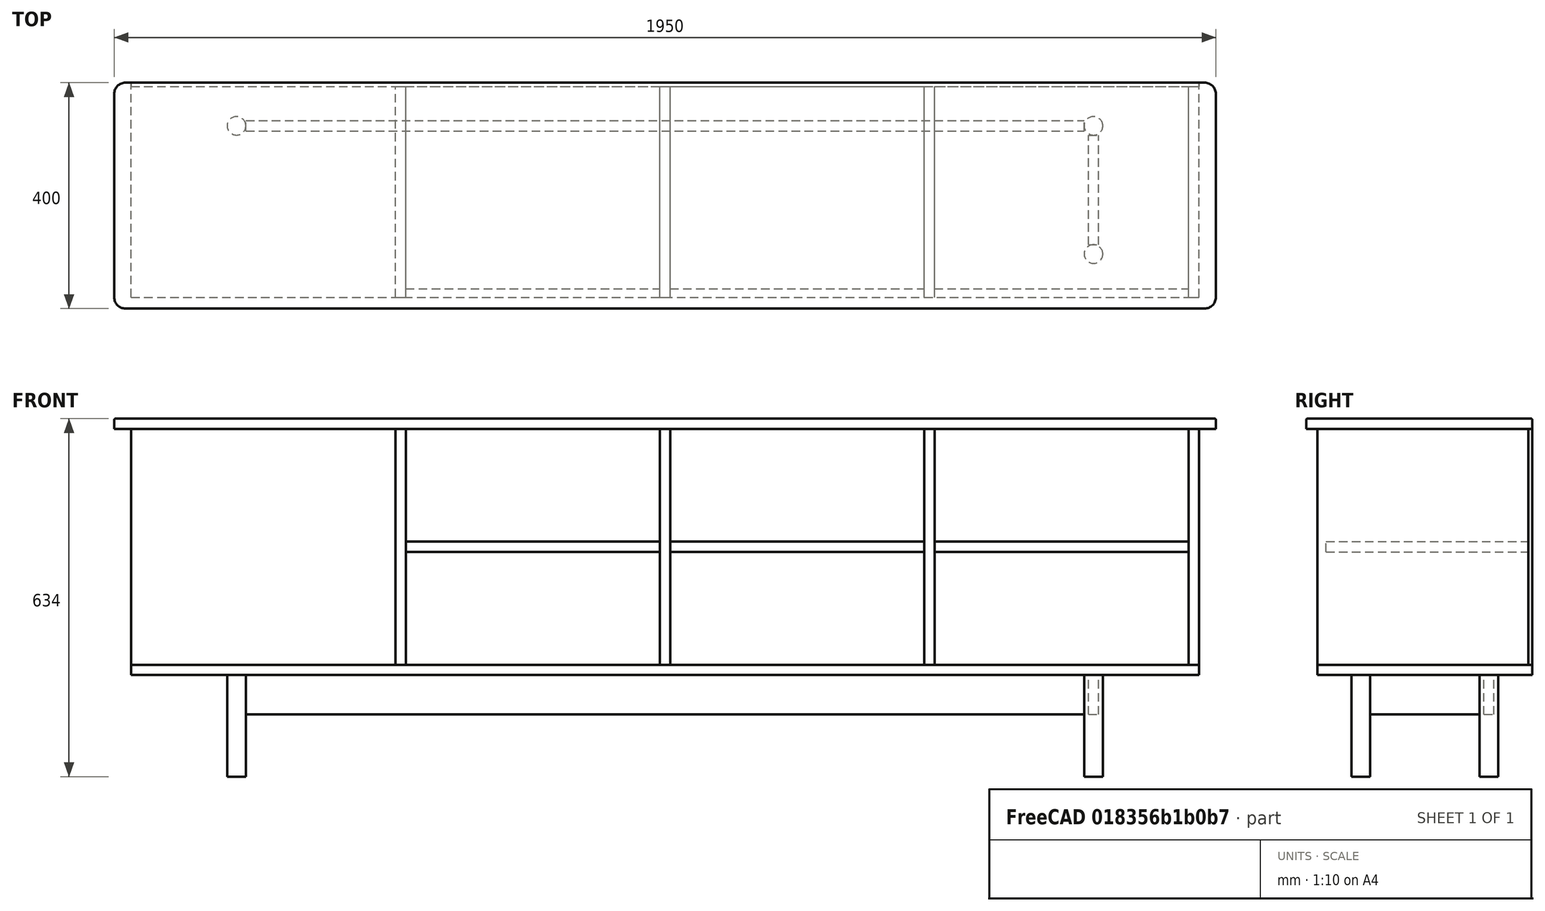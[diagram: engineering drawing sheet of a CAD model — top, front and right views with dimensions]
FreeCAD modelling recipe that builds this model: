
FCSTD DOCUMENT  (FreeCAD 0.20RUnknown)
Label: tv-furniture
License: All rights reserved
LicenseURL: http://en.wikipedia.org/wiki/All_rights_reserved
objects: Part::FeaturePython×12, Part::Box×7, Spreadsheet::Sheet×2, Part::Fillet×2, Part::Cylinder×1, TechDraw::DrawSVGTemplate×1, TechDraw::DrawViewSpreadsheet×1, TechDraw::DrawPage×1
note: 22 computed .brp shape members not serialized (recipe doc carries the construction recipe); baked Part::Feature solids carry a one-line shape summary decoded from their .brp

FEATURE [Part::Box] Box028  label="Top"
  AttacherType = Attacher::AttachEngine3D
  Height = 18
  Length = 1950
  Placement = pos=(-30,-20,436) rot=(0,0,1;0rad)
  Texture_Fit = biggest surface
  Texture_Repeat_X = 1
  Texture_Repeat_Y = 1
  Texture_Rotation = 0
  Texture_URL = <userpath>/Hentet/grantræ.jpg
  Width = 400
  expr: .Placement.Base.x = -<<Spreadsheet>>.TopBreddeMargin
  expr: .Placement.Base.y = -<<Spreadsheet>>.TopDybdeMargin
  expr: .Placement.Base.z = <<Spreadsheet>>.Hoejde - <<Spreadsheet>>.Plade
  expr: Height = <<Spreadsheet>>.TopPlade
  expr: Length = <<Spreadsheet>>.Bredde + 2 * <<Spreadsheet>>.TopBreddeMargin
FEATURE [Part::Box] Box029  label="Side/Skillevæg"
  AttacherType = Attacher::AttachEngine3D
  Height = 418
  Length = 18
  Placement = pos=(0,0,18) rot=(0,0,1;0rad)
  Texture_Fit = biggest surface
  Texture_Repeat_X = 1
  Texture_Repeat_Y = 1
  Texture_Rotation = 0
  Texture_URL = <userpath>/Hentet/grantræ.jpg
  Width = 373
  expr: .Placement.Base.z = <<Spreadsheet>>.Plade
  expr: Height = <<Spreadsheet>>.Hoejde - <<Spreadsheet>>.Plade * 2
  expr: Length = <<Spreadsheet>>.Plade
  expr: Width = <<Spreadsheet>>.Dybde - <<Spreadsheet>>.BagPlade
FEATURE [Part::Box] Box034  label="Hylde"
  AttacherType = Attacher::AttachEngine3D
  Height = 18
  Length = 450
  Placement = pos=(18,15,218) rot=(0,0,1;0rad)
  Texture_Fit = biggest surface
  Texture_Repeat_X = 1
  Texture_Repeat_Y = 1
  Texture_Rotation = 0
  Texture_URL = <userpath>/Hentet/grantræ.jpg
  Width = 358
  expr: .Placement.Base.x = <<Side/Skillevæg>>.Placement.Base.x + <<Spreadsheet>>.Plade
  expr: .Placement.Base.y = <<Spreadsheet>>.HyldeMellemrum
  expr: .Placement.Base.z = <<Spreadsheet>>.Plade + <<Spreadsheet>>.KasseHoejde
  expr: Height = <<Spreadsheet>>.Plade
  expr: Length = <<Spreadsheet>>.KasseBredde
  expr: Width = <<Spreadsheet>>.Dybde - <<Spreadsheet>>.HyldeMellemrum - <<Spreadsheet>>.BagPlade
FEATURE [Part::Box] Box035  label="Bund"
  AttacherType = Attacher::AttachEngine3D
  Height = 18
  Length = 1890
  Texture_Fit = biggest surface
  Texture_Repeat_X = 1
  Texture_Repeat_Y = 1
  Texture_Rotation = 0
  Texture_URL = <userpath>/Hentet/grantræ.jpg
  Width = 380
  expr: .Placement.Base.z = 0
  expr: Height = <<Spreadsheet>>.Plade
  expr: Length = <<Spreadsheet>>.Bredde
  expr: Width = <<Spreadsheet>>.Dybde
FEATURE [Part::Box] Box039  label="Sokkel X"
  AttacherType = Attacher::AttachEngine3D
  Height = 70
  Length = 1484
  Placement = pos=(203,67.5,-70) rot=(0,0,1;0rad)
  Texture_Fit = biggest surface
  Texture_Repeat_X = 1
  Texture_Repeat_Y = 1
  Texture_Rotation = 0
  Texture_URL = <userpath>/Hentet/grantræ.jpg
  Width = 18
  expr: .Placement.Base.x = <<Ben>>.Placement.Base.x + <<Ben>>.Radius
  expr: .Placement.Base.y = <<Ben>>.Placement.Base.y - <<Spreadsheet>>.Plade / 2
  expr: .Placement.Base.z = -<<Spreadsheet>>.SokkelHoejde
  expr: Height = <<Spreadsheet>>.SokkelHoejde
  expr: Length = <<Ben002>>.Placement.Base.x - <<Ben>>.Placement.Base.x - 2 * <<Spreadsheet>>.BenRadius
  expr: Width = <<Spreadsheet>>.Plade
FEATURE [Part::Cylinder] Cylinder008  label="Ben"
  Angle = 360
  AttacherType = Attacher::AttachEngine3D
  FirstAngle = 0
  Height = 180
  Placement = pos=(186.5,76.5,-180) rot=(0,0,1;0rad)
  Radius = 16.5
  SecondAngle = 0
  Texture_Fit = biggest surface
  Texture_Repeat_X = 1
  Texture_Repeat_Y = 1
  Texture_Rotation = 0
  Texture_URL = <userpath>/Hentet/grantræ.jpg
  expr: .Placement.Base.x = <<Spreadsheet>>.SokkelBreddeMargin + Radius
  expr: .Placement.Base.y = <<Spreadsheet>>.SokkelDybdeMargin + Radius
  expr: .Placement.Base.z = -<<Spreadsheet>>.BenHoejde
  expr: Radius = Spreadsheet002.BenRadius
FEATURE [Spreadsheet::Sheet] Spreadsheet002  label="Spreadsheet"
  cells = A1=Kassebredde; B1=Kassehøjde; C1=Dybde; D1=Plade; E1=Grundbredde; F1=Grundhøjde; G1=Topplade breddemargin; H1=Topplade dybdemargin; I1=Sokkel højde; J1=Sokkel breddemargin; K1=Sokkel dybdemargin; A2(KasseBredde)==45cm; B2(KasseHoejde)==20cm; C2(Dybde)==38cm; D2(Plade)==1.8cm; E2(Bredde)==A2 * 4 + D2 * 5; F2(Hoejde)==B2 * 2 + D2 * 3; G2(TopBreddeMargin)==3cm; H2(TopDybdeMargin)==2cm; I2(SokkelHoejde)==7cm; J2(SokkelBreddeMargin)==17cm; K2(SokkelDybdeMargin)==6cm; D3(TopPlade)==18mm; A4=Benhøjde; B4=Ben radius; D4(BagPlade)==7mm; A5(BenHoejde)==18cm; B5(BenRadius)==33mm / 2; A7=Hylde mellemrum; A8(HyldeMellemrum)==1.5cm; A13=Type; B13=Mål; C13=Antal; D13=Bauhaus; E13=Silvan; A14=Limtræ; B14=400*2000*18; C14=4; D14==229.95 * C14; E14==C14 * 229.95; A15=Finér bauhaus; B15=800*1200*6; C15=2; D15==189.95 * C15; A16=Finér silvan; B16=2440*1220*6,5; C16=1; E16==C16 * 339.95; A17=Rundstok; B17=Ø33 x 2100; C17=1; D17==C17 * 124.95; E17=129.95; A19=I alt; D19==D14 + D15 + D17; E19==E14 + E16 + E17
FEATURE [Part::Box] panelXY  label="Bagplade"
  AttacherType = Attacher::AttachEngine3D
  Height = 7
  Length = 1890
  Placement = pos=(0,380,18) rot=(1,0,0;1.5708rad)
  Texture_Fit = biggest surface
  Texture_Repeat_X = 1
  Texture_Repeat_Y = 1
  Texture_Rotation = 0
  Texture_URL = <userpath>/Hentet/grantræ.jpg
  Width = 418
  expr: .Placement.Base.y = <<Spreadsheet>>.Dybde
  expr: .Placement.Base.z = <<Spreadsheet>>.Plade
  expr: Height = <<Spreadsheet>>.BagPlade
  expr: Length = <<Spreadsheet>>.Bredde
  expr: Width = <<Spreadsheet>>.KasseHoejde * 2 + <<Spreadsheet>>.Plade
FEATURE [Part::Box] Box041  label="Sokkel Y"
  AttacherType = Attacher::AttachEngine3D
  Height = 70
  Length = 18
  Placement = pos=(177.5,93,-70) rot=(0,0,1;0rad)
  Texture_Fit = biggest surface
  Texture_Repeat_X = 1
  Texture_Repeat_Y = 1
  Texture_Rotation = 0
  Texture_URL = <userpath>/Hentet/grantræ.jpg
  Width = 194
  expr: .Placement.Base.x = <<Ben001>>.Placement.Base.x - <<Spreadsheet>>.Plade / 2
  expr: .Placement.Base.y = <<Ben>>.Placement.Base.y + <<Spreadsheet>>.BenRadius
  expr: .Placement.Base.z = -<<Spreadsheet>>.SokkelHoejde
  expr: Height = <<Spreadsheet>>.SokkelHoejde
  expr: Length = <<Spreadsheet>>.Plade
  expr: Width = <<Ben001>>.Placement.Base.y - <<Ben>>.Placement.Base.y - 2 * <<Spreadsheet>>.BenRadius
FEATURE [Part::Fillet] Fillet004
  Base = -> Box028
  Edges = 4 edges r=20: [Edge1,Edge3,Edge5,Edge7]
FEATURE [Part::Fillet] Fillet005
  Base = -> Fillet004
  Edges = 8 edges r=2: [Edge1,Edge5,Edge6,Edge7,Edge8,Edge9,Edge10,Edge11]
FEATURE [Part::FeaturePython] Clone  label="Side/Skillevæg001"  # Draft clone (typed FeaturePython)
  AttacherType = Attacher::AttachEngine3D
  Fuse = false
  Objects = -> [Box029]
  Placement = pos=(468,0,18) rot=(0,0,1;0rad)
  Scale = (1,1,1)
  expr: .Placement.Base.x = <<Spreadsheet>>.Plade + <<Spreadsheet>>.KasseBredde
  expr: .Placement.Base.z = <<Spreadsheet>>.Plade
FEATURE [Part::FeaturePython] Clone001  label="Side/Skillevæg002"  # Draft clone (typed FeaturePython)
  AttacherType = Attacher::AttachEngine3D
  Fuse = false
  Objects = -> [Box029]
  Placement = pos=(936,0,18) rot=(0,0,1;0rad)
  Scale = (1,1,1)
  expr: .Placement.Base.x = <<Spreadsheet>>.Plade * 2 + <<Spreadsheet>>.KasseBredde * 2
  expr: .Placement.Base.z = <<Spreadsheet>>.Plade
FEATURE [Part::FeaturePython] Clone002  label="Side/Skillevæg003"  # Draft clone (typed FeaturePython)
  AttacherType = Attacher::AttachEngine3D
  Fuse = false
  Objects = -> [Box029]
  Placement = pos=(1404,0,18) rot=(0,0,1;0rad)
  Scale = (1,1,1)
  expr: .Placement.Base.x = <<Spreadsheet>>.Plade * 3 + <<Spreadsheet>>.KasseBredde * 3
  expr: .Placement.Base.z = <<Spreadsheet>>.Plade
FEATURE [Part::FeaturePython] Clone003  label="Side/Skillevæg004"  # Draft clone (typed FeaturePython)
  AttacherType = Attacher::AttachEngine3D
  Fuse = false
  Objects = -> [Box029]
  Placement = pos=(1872,0,18) rot=(0,0,1;0rad)
  Scale = (1,1,1)
  expr: .Placement.Base.x = <<Spreadsheet>>.Bredde - <<Spreadsheet>>.Plade
  expr: .Placement.Base.z = <<Spreadsheet>>.Plade
FEATURE [Part::FeaturePython] Clone004  label="Hylde001"  # Draft clone (typed FeaturePython)
  AttacherType = Attacher::AttachEngine3D
  Fuse = false
  Objects = -> [Box034]
  Placement = pos=(486,15,218) rot=(0,0,1;0rad)
  Scale = (1,1,1)
  expr: .Placement.Base.x = <<Side/Skillevæg001>>.Placement.Base.x + <<Spreadsheet>>.Plade
  expr: .Placement.Base.y = <<Spreadsheet>>.HyldeMellemrum
  expr: .Placement.Base.z = <<Spreadsheet>>.Plade + <<Spreadsheet>>.KasseHoejde
FEATURE [Part::FeaturePython] Clone005  label="Hylde002"  # Draft clone (typed FeaturePython)
  AttacherType = Attacher::AttachEngine3D
  Fuse = false
  Objects = -> [Box034]
  Placement = pos=(954,15,218) rot=(0,0,1;0rad)
  Scale = (1,1,1)
  expr: .Placement.Base.x = <<Side/Skillevæg002>>.Placement.Base.x + <<Spreadsheet>>.Plade
  expr: .Placement.Base.y = <<Spreadsheet>>.HyldeMellemrum
  expr: .Placement.Base.z = <<Spreadsheet>>.Plade + <<Spreadsheet>>.KasseHoejde
FEATURE [Part::FeaturePython] Clone006  label="Hylde003"  # Draft clone (typed FeaturePython)
  AttacherType = Attacher::AttachEngine3D
  Fuse = false
  Objects = -> [Box034]
  Placement = pos=(1422,15,218) rot=(0,0,1;0rad)
  Scale = (1,1,1)
  expr: .Placement.Base.x = <<Side/Skillevæg003>>.Placement.Base.x + <<Spreadsheet>>.Plade
  expr: .Placement.Base.y = <<Spreadsheet>>.HyldeMellemrum
  expr: .Placement.Base.z = <<Spreadsheet>>.Plade + <<Spreadsheet>>.KasseHoejde
FEATURE [Part::FeaturePython] Clone007  label="Sokkel X001"  # Draft clone (typed FeaturePython)
  AttacherType = Attacher::AttachEngine3D
  Fuse = false
  Objects = -> [Box039]
  Placement = pos=(203,294.5,-70) rot=(0,0,1;0rad)
  Scale = (1,1,1)
  expr: .Placement.Base.x = <<Ben>>.Placement.Base.x + <<Ben>>.Radius
  expr: .Placement.Base.y = <<Ben001>>.Placement.Base.y - <<Spreadsheet>>.Plade / 2
  expr: .Placement.Base.z = -<<Spreadsheet>>.SokkelHoejde
FEATURE [Part::FeaturePython] Clone008  label="Sokkel Y001"  # Draft clone (typed FeaturePython)
  AttacherType = Attacher::AttachEngine3D
  Fuse = false
  Objects = -> [Box041]
  Placement = pos=(1694.5,93,-70) rot=(0,0,1;0rad)
  Scale = (1,1,1)
  expr: .Placement.Base.x = <<Ben003>>.Placement.Base.x - <<Spreadsheet>>.Plade / 2
  expr: .Placement.Base.y = <<Ben>>.Placement.Base.y + <<Spreadsheet>>.BenRadius
  expr: .Placement.Base.z = -<<Spreadsheet>>.SokkelHoejde
FEATURE [Part::FeaturePython] Clone009  label="Ben001"  # Draft clone (typed FeaturePython)
  AttacherType = Attacher::AttachEngine3D
  Fuse = false
  Objects = -> [Cylinder008]
  Placement = pos=(186.5,303.5,-180) rot=(0,0,1;0rad)
  Scale = (1,1,1)
  expr: .Placement.Base.x = <<Spreadsheet>>.SokkelBreddeMargin + <<Spreadsheet>>.BenRadius
  expr: .Placement.Base.y = <<Spreadsheet>>.Dybde - <<Spreadsheet>>.SokkelDybdeMargin - <<Spreadsheet>>.BenRadius
  expr: .Placement.Base.z = -<<Spreadsheet>>.BenHoejde
FEATURE [Part::FeaturePython] Clone010  label="Ben002"  # Draft clone (typed FeaturePython)
  AttacherType = Attacher::AttachEngine3D
  Fuse = false
  Objects = -> [Cylinder008]
  Placement = pos=(1703.5,76.5,-180) rot=(0,0,1;0rad)
  Scale = (1,1,1)
  expr: .Placement.Base.x = <<Spreadsheet>>.Bredde - <<Spreadsheet>>.SokkelBreddeMargin - <<Spreadsheet>>.BenRadius
  expr: .Placement.Base.y = <<Spreadsheet>>.SokkelDybdeMargin + <<Spreadsheet>>.BenRadius
  expr: .Placement.Base.z = -<<Spreadsheet>>.BenHoejde
FEATURE [Part::FeaturePython] Clone011  label="Ben003"  # Draft clone (typed FeaturePython)
  AttacherType = Attacher::AttachEngine3D
  Fuse = false
  Objects = -> [Cylinder008]
  Placement = pos=(1703.5,303.5,-180) rot=(0,0,1;0rad)
  Scale = (1,1,1)
  expr: .Placement.Base.x = <<Spreadsheet>>.Bredde - <<Spreadsheet>>.SokkelBreddeMargin - <<Spreadsheet>>.BenRadius
  expr: .Placement.Base.y = <<Spreadsheet>>.Dybde - <<Spreadsheet>>.SokkelDybdeMargin - <<Spreadsheet>>.BenRadius
  expr: .Placement.Base.z = -<<Spreadsheet>>.BenHoejde
FEATURE [Spreadsheet::Sheet] toCut
  cells = A1=Name; B1=Dimensions; E1=Thickness; F1=Quantity; G1=m2; A2=Top; B2==400mm; C2=x; D2==1950mm; E2==18mm; F2=1; G2=0.78; A3=Side/Skillevæg; B3==373mm; C3=x; D3==418mm; E3==18mm; F3=5; G3=0.77957; A4=Hylde; B4==358mm; C4=x; D4==450mm; E4==18mm; F4=4; G4=0.6444; A5=Bund; B5==380mm; C5=x; D5==1890mm; E5==18mm; F5=1; G5=0.7181999999999999; A6=Sokkel X; B6==70mm; C6=x; D6==1484mm; E6==18mm; F6=2; G6=0.20776; A7=Bagplade; B7==418mm; C7=x; D7==1890mm; E7==7mm; F7=1; G7=0.7900199999999999; A8=Sokkel Y; B8==70mm; C8=x; D8==194mm; E8==18mm; F8=2; G8=0.02716; A9=Summary by thickness; E10==18mm; F10=15; G10=3.15709; E11==7mm; F11=1; G11=0.7900199999999999; A13=Edge size; G13==35.502m; A15=4 x ; B15=Mounting points, 33.0 x 180; B16=Diameter; E16==33mm; B17=Length; E17==180mm; A19=Generated by FreeCAD macro: github.com/dprojects/getDimensions
FEATURE [TechDraw::DrawSVGTemplate] Template
  Height = 297
  Orientation = 0
  Width = 210
FEATURE [TechDraw::DrawViewSpreadsheet] Sheet
  CellEnd = G20
  CellStart = A1
  Font = DejaVu Sans
  LineWidth = 0.1
  LockPosition = false
  Rotation = 0
  ScaleType = 2
  Source = -> toCut
  Symbol = <blob: 19245 chars omitted>
  TextSize = 13
  X = 100.684
  Y = 141.186
FEATURE [TechDraw::DrawPage] toPrint
  KeepUpdated = true
  NextBalloonIndex = 1
  ProjectionType = 0
  Template = -> Template
  Views = -> [Sheet]
